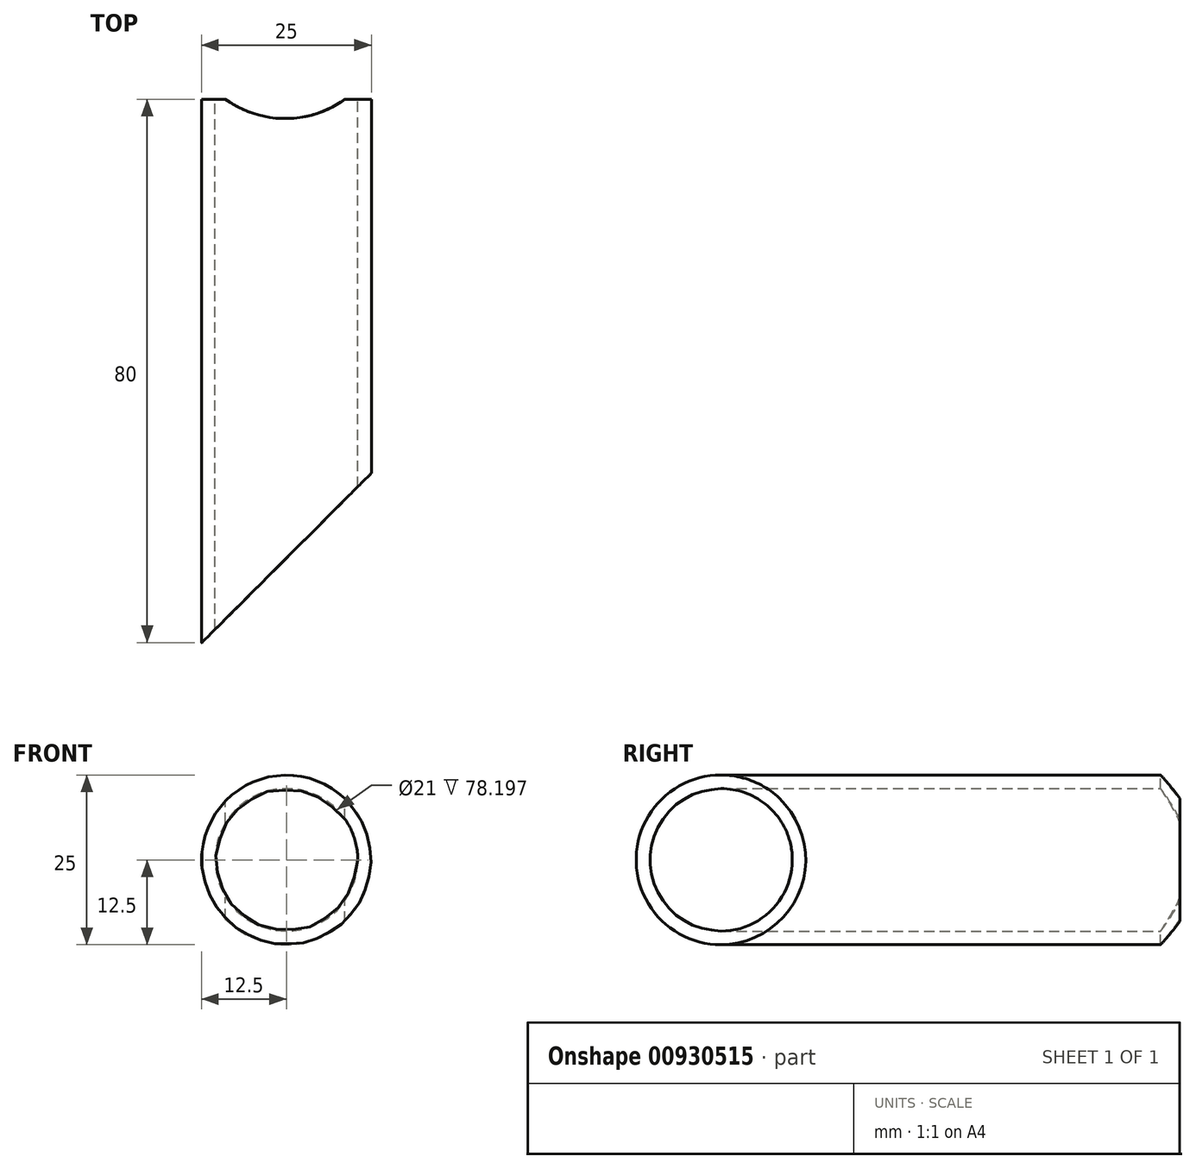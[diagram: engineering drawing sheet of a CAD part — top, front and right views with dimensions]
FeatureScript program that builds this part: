
annotation { "Feature Type Name" : "Feature", "Feature Type Description" : "" }
export const myFeature = defineFeature(function(context is Context, id is Id, definition is map)
    precondition{}
    {
        {
            var Q0;
            Q0=qCreatedBy(makeId("Front.planeOp"),FACE);
            var sketch = newSketch(context, id + "F0", { "sketchPlane" : qUnion([Q0])});
            skCircle(sketch, "E0", {"center": v(0, 0) * mm, "radius": 12.5 * mm});
            skCircle(sketch, "E1", {"center": v(0, 0) * mm, "radius": 10.5 * mm});
            skSolve(sketch);
        }
        {
            var Q0;
            Q0=qSketchRegion(id+"F0",true);
            extrude(context, id + "F1", {"entities" : qUnion([Q0]), "depth" : 80 * mm, "offsetDistance" : 25 * mm});
        }
        {
            var Q0;
            Q0=qCreatedBy(makeId("Top.planeOp"),FACE);
            var sketch = newSketch(context, id + "F2", { "sketchPlane" : qUnion([Q0])});
            skLineSegment(sketch, "E2", {"start": v(-12.5, -80.05) * mm, "end": v(12.5, -80.05) * mm});
            skLineSegment(sketch, "E3", {"start": v(12.5, -80.05) * mm, "end": v(12.5, -55.05) * mm});
            skLineSegment(sketch, "E4", {"start": v(12.5, -55.05) * mm, "end": v(-12.5, -80.05) * mm});
            skSolve(sketch);
        }
        {
            var Q0;
            Q0=qSketchRegion(id+"F2",true);
            extrude(context, id + "F3", {"entities" : qUnion([Q0]), "operationType" : NewBodyOperationType.REMOVE, "endBound" : BoundingType.SYMMETRIC, "depth" : 25 * mm, "offsetDistance" : 25 * mm});
        }
        {
            var Q0;
            Q0=qCreatedBy(makeId("Top.planeOp"),FACE);
            var sketch = newSketch(context, id + "F4", { "sketchPlane" : qUnion([Q0])});
            skArc(sketch, "E5", {"start": v(-8.97, 0) * mm, "mid": v(-0.18, -2.84) * mm, "end": v(8.6, 0) * mm});
            skLineSegment(sketch, "E6", {"start": v(-8.97, 0) * mm, "end": v(8.6, 0) * mm});
            skSolve(sketch);
        }
        {
            var Q0;
            Q0 = qSketchRegion(id + "F4", true);
            extrude(context, id + "F5", {"entities" : qUnion([Q0]), "operationType" : NewBodyOperationType.REMOVE, "endBound" : BoundingType.SYMMETRIC, "oppositeDirection" : true, "depth" : 50 * mm, "offsetDistance" : 25 * mm});
        }
    });
